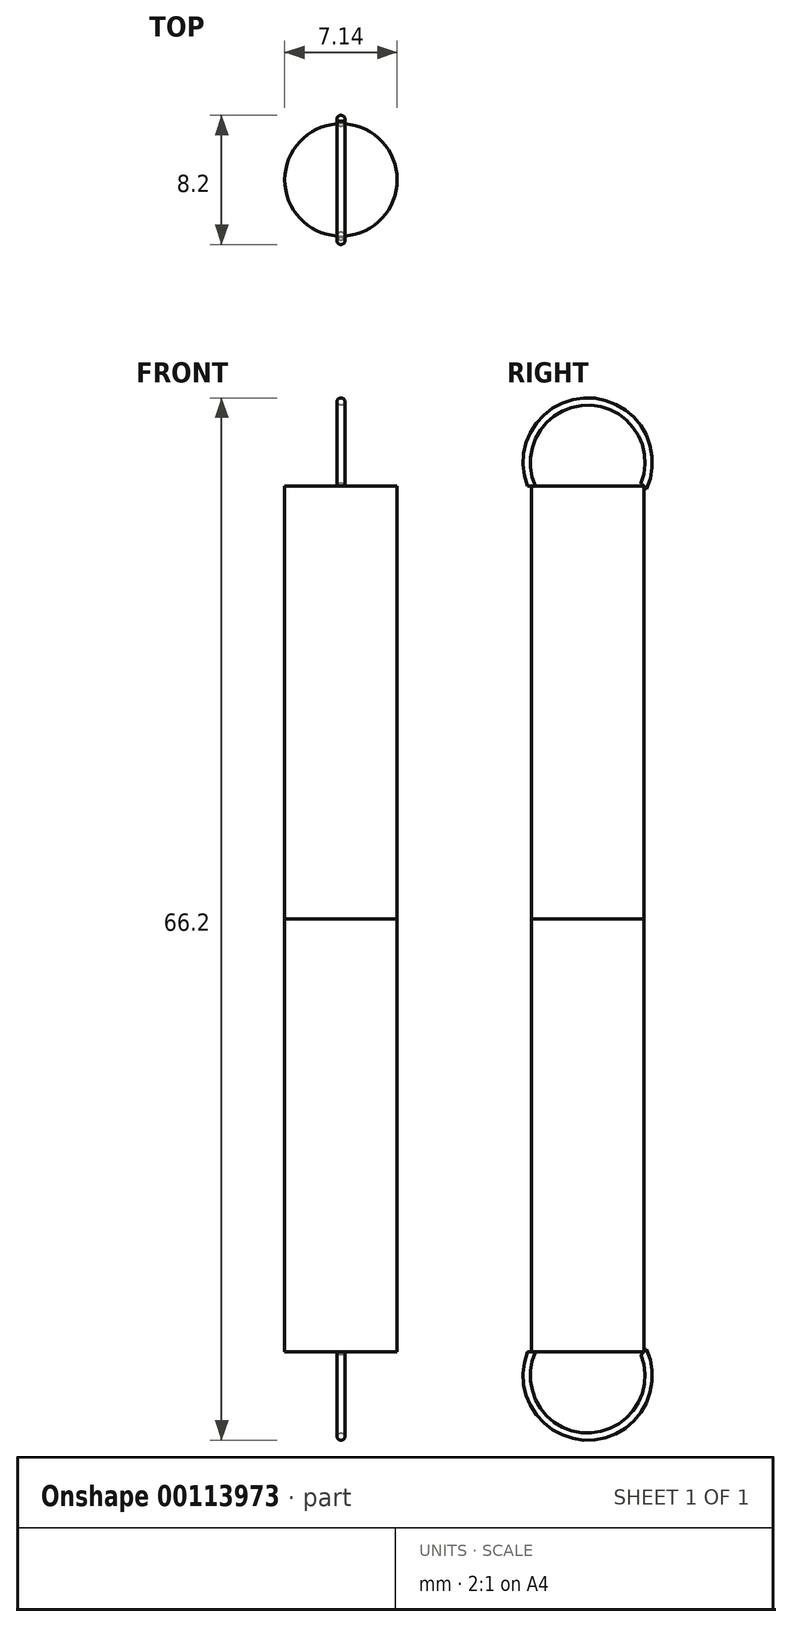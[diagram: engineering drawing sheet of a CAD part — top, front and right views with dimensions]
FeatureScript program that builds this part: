
annotation { "Feature Type Name" : "Feature", "Feature Type Description" : "" }
export const myFeature = defineFeature(function(context is Context, id is Id, definition is map)
    precondition{}
    {
        {
            var Q0;
            Q0=qCreatedBy(makeId("Top.planeOp"),FACE);
            var sketch = newSketch(context, id + "F0", { "sketchPlane" : qUnion([Q0])});
            skCircle(sketch, "E0", {"center": v(0, 0) * mm, "radius": 3.57 * mm});
            skSolve(sketch);
        }
        {
            var Q0;
            Q0 = qSketchRegion(id + "F0", true);
            extrude(context, id + "F1", {"entities" : qUnion([Q0]), "depth" : 27.5 * mm});
        }
        {
            var Q0;
            Q0=qCreatedBy(makeId("Right.planeOp"),FACE);
            var sketch = newSketch(context, id + "F2", { "sketchPlane" : qUnion([Q0])});
            skArc(sketch, "E1", {"start": v(3.57, 27.5) * mm, "mid": v(0, 32.87) * mm, "end": v(-3.57, 27.5) * mm});
            skLineSegment(sketch, "E2", {"start": v(-3.57, 27.5) * mm, "end": v(3.57, 27.5) * mm});
            skSolve(sketch);
        }
        {
            var Q0;
            Q0=makeQuery(id+"F1.opExtrude","CAP_FACE",FACE,{"disambiguationData":[OSD([sQuery(id+"F0.wireOp",EDGE,"E0")])],"isStart":false});
            var sketch = newSketch(context, id + "F3", { "sketchPlane" : qUnion([Q0])});
            skCircle(sketch, "E3", {"center": v(0, -3.57) * mm, "radius": 0.25 * mm});
            skSolve(sketch);
        }
        {
            var Q0;
            {var subQ0=sQuery(id+"F3.wireOp",EDGE,"E3");var subQ1=makeQuery(id+"F1.opExtrude","CAP_EDGE",EDGE,{"disambiguationData":[OSD([sQuery(id+"F0.wireOp",EDGE,"E0")])],"isStart":false});var subQ2=makeQuery(id+"F3.imprint","INTERSECT",VERTEX,{"disambiguationData":[OD(0.0)],"derivedFrom":[subQ1,subQ0]});Q0=makeQuery(id+"F3.imprint","IMPRINT",FACE,{"disambiguationData":[TD([[makeQuery(id+"F3.imprint","IMPRINT",EDGE,{"disambiguationData":[TD([[subQ2,-1.0]])],"derivedFrom":subQ0}),1.0]])]});}
            var Q1;
            {var subQ0=sQuery(id+"F3.wireOp",EDGE,"E3");var subQ1=makeQuery(id+"F1.opExtrude","CAP_EDGE",EDGE,{"disambiguationData":[OSD([sQuery(id+"F0.wireOp",EDGE,"E0")])],"isStart":false});var subQ2=makeQuery(id+"F3.imprint","INTERSECT",VERTEX,{"disambiguationData":[OD(0.0)],"derivedFrom":[subQ1,subQ0]});Q1=makeQuery(id+"F3.imprint","IMPRINT",FACE,{"disambiguationData":[TD([[makeQuery(id+"F3.imprint","IMPRINT",EDGE,{"disambiguationData":[TD([[subQ2,1.0]])],"derivedFrom":subQ0}),1.0]])]});}
            var Q2;
            Q2=sQuery(id+"F2.wireOp",EDGE,"E1");
            sweep(context, id + "F4", {"profiles" : qUnion([Q0, Q1]), "path" : qUnion([Q2])});
        }
        {
            var Q0;
            Q0=makeQuery(id+"F4.opSweep","SWEPT_BODY",BODY,{"disambiguationData":[OSD([sQuery(id+"F2.wireOp",EDGE,"E1"),sQuery(id+"F3.wireOp",EDGE,"E3")])]});
            var Q1;
            Q1=makeQuery(id+"F1.opExtrude","SWEPT_BODY",BODY,{"disambiguationData":[OSD([sQuery(id+"F0.wireOp",EDGE,"E0")])]});
            var Q2;
            Q2=qCreatedBy(makeId("Top.planeOp"),FACE);
            mirror(context, id + "F5", {"entities" : qUnion([Q0, Q1]), "mirrorPlane" : qUnion([Q2])});
        }
        {
            var Q0;
            Q0=qCreatedBy(makeId("Right.planeOp"),FACE);
            var sketch = newSketch(context, id + "F6", { "sketchPlane" : qUnion([Q0])});
            skCircle(sketch, "E4", {"center": v(0, 29) * mm, "radius": 1.23 * mm});
            skSolve(sketch);
        }
        {
            var Q0;
            Q0 = qSketchRegion(id + "F6", true);
            var Q1;
            Q1=sQuery(id+"F6.wireOp",EDGE,"E4");
            extrude(context, id + "F7", {"entities" : qUnion([Q0]), "bodyType" : ToolBodyType.SURFACE, "surfaceEntities" : qUnion([Q1]), "endBound" : BoundingType.SYMMETRIC, "depth" : 5 * mm});
        }
    });
